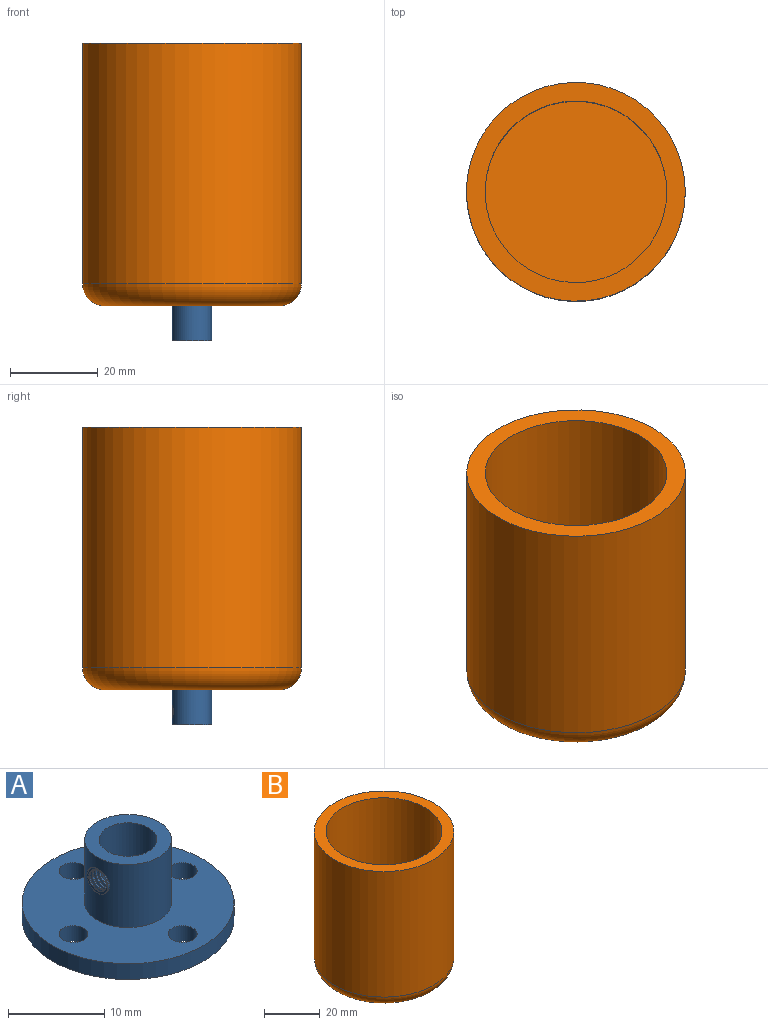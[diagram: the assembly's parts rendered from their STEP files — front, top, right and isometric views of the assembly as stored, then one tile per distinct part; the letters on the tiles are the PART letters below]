
ASSEMBLY  parts=2 mates=1
PART A: 20 faces, bbox 22.1x22.1x10.1 mm
  f0: cylinder r=4.5mm len=9mm, axis (0,0,-1), area 218.7mm2, adj f6,f9,f11,f12
  f1: cylinder r=1.5mm len=3mm, axis (0,0,-1), area 18.8mm2, adj f6,f7
  f2: cylinder r=1.5mm len=3mm, axis (0,0,-1), area 18.8mm2, adj f6,f7
  f3: cylinder r=1.5mm len=3mm, axis (0,0,-1), area 18.8mm2, adj f6,f7
  f4: cylinder r=1.5mm len=3mm, axis (0,0,-1), area 18.8mm2, adj f6,f7
  f5: cylinder r=11mm len=22mm, axis (0,0,-1), area 138.2mm2, adj f6,f7
  f6: plane 22x22mm, normal (0,0,1), area 288.2mm2, adj f0,f1,f2,f3,f4,f5
  f7: plane 22x22mm, normal (0,0,-1), area 323.6mm2, adj f1,f2,f3,f4,f5,f8
  f8: cylinder r=3mm len=10mm, axis (0,0,-1), area 180.9mm2, adj f7,f9,f10,f13,f16
  f9: plane 9x9mm, normal (0,0,1), area 35.3mm2, adj f0,f8
  f10: cylinder r=1.53mm len=3mm, axis (-1,0,0), area 0.9mm2, adj f8,f13
  f11: cylinder r=1.53mm len=3.06mm, axis (-1,0,0), area 0.6mm2, adj f0,f14
  f12: cylinder r=1.53mm len=3.06mm, axis (-1,0,0), area 0.6mm2, adj f0,f14
  f13: plane 3.13x3.07mm, normal (1,0,0), area 1.4mm2, adj f8,f10,f15,f16,f17,f18,f19
  f14: plane 3.13x3.13mm, normal (-1,0,0), area 1.4mm2, adj f11,f12,f15,f17,f18,f19
  f15: cylinder r=1.25mm len=2.5mm, axis (-1,0,0), area 5.5mm2, adj f13,f14,f17,f18
  f16: cylinder r=1.53mm len=3mm, axis (-1,0,0), area 0.9mm2, adj f8,f13
  f17: bspline ~3.46x3mm, area 8.5mm2, adj f13,f14,f15,f19
  f18: bspline ~3.46x3mm, area 8.5mm2, adj f13,f14,f15,f19
  f19: cylinder r=1.5mm len=3mm, axis (1,0,0), area 6.8mm2, adj f13,f14,f17,f18
PART B: 16 faces, bbox 54.1x54.1x60 mm
  f0: cylinder r=20.75mm len=50mm, axis (0,0,-1), area 6518.8mm2, adj f2,f3
  f1: cylinder r=25mm len=55mm, axis (0,0,-1), area 8639.4mm2, adj f2,f15
  f2: plane 50x50mm, normal (0,0,1), area 610.8mm2, adj f0,f1
  f3: plane 41.5x41.5mm, normal (0,0,1), area 1352.7mm2, adj f0
  f4: plane 40x40mm, normal (0,0,-1), area 876.5mm2, adj f5,f15
  f5: cylinder r=11mm len=22mm, axis (0,0,-1), area 138.2mm2, adj f4,f6
  f6: plane 22x22mm, normal (0,0,-1), area 360.5mm2, adj f5,f7,f9,f11,f13
  f7: cylinder r=1.25mm len=5mm, axis (0,0,-1), area 39.3mm2, adj f6,f8
  f8: plane 2.5x2.5mm, normal (0,0,-1), area 4.9mm2, adj f7
  f9: cylinder r=1.25mm len=5mm, axis (0,0,-1), area 39.3mm2, adj f6,f10
  f10: plane 2.5x2.5mm, normal (0,0,-1), area 4.9mm2, adj f9
  f11: cylinder r=1.25mm len=5mm, axis (0,0,-1), area 39.3mm2, adj f6,f12
  f12: plane 2.5x2.5mm, normal (0,0,-1), area 4.9mm2, adj f11
  f13: cylinder r=1.25mm len=5mm, axis (0,0,-1), area 39.3mm2, adj f6,f14
  f14: plane 2.5x2.5mm, normal (0,0,-1), area 4.9mm2, adj f13
  f15: torus R=20mm, axis (0,0,1), area 1144mm2, adj f1,f4
PLACE A rot(axis=(0.71,-0.71,0),180deg) t=(-37.22,-18.04,-7.83)mm
PLACE B t=(-37.22,-18.04,0.17)mm
MATE fastened A.f2 <-> B.f11  axis (0,0,1) through (-29.22,-18.04,-7.83)mm
